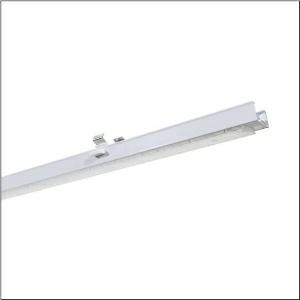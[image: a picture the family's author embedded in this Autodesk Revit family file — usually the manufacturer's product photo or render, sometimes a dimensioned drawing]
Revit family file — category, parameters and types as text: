
# Revit family: sanierungs-leuchteneinsatz_31_gen_2_51re11mb4cb_9c12
name_source: partatom
category: Lighting Fixtures
units: mm (PartAtom-declared; Revit-internal decimal feet)

## family parameters
Cut with Voids When Loaded = No
Host = Face
Light Source = No
Part Type = Normal
Room Calculation Point = No
Round Connector Dimension = Use Diameter
Shared = No

## types (1)
- --- (1 x LED, 11500 lm, 66 W, 4000K)
    Apparent Load = 66 VA
    CIE Flux Codes = 83 93 98 100 100
    Color Rendering = 80
    Color Temperature = 4000K
    Default Elevation = 1800 mm
    Description = Refurbishment luminaire insert Gen.2, luminaire insert, of extruded aluminium section, coated, traffic white (RAL 9016), length: 1.472mm, width: 91mm, height: 53mm, LED rated luminous flux: 11.500lm, light colour: 840, control gear: ON/OFF Multilumen, control gear: ECG Multilumen, with system connector: socket, mains connection: 220..240V, AC, 50/60Hz, connected load according to luminous flux setting (19/24/32/37/47/52/60/66W), luminous flux adjustable on luminaire in eight steps (3450/4380/5800/6700/8350/9200/10500/11500lm ), primary light control with lens, of plastic, primary optical cover: cover, of PMMA, light emission: direct distribution, protection rating (complete): IP20, insulation class (complete): insulation class I (protective earthing), certification: CE, UKCA, permissible ambient temperature for indoor applications: -20..+40°C, packaging unit: 1 piece
    Height = 58 mm
    Lamp = 1 x LED
    Lamp Light Flux = 11500 lm
    Lamp Power = 66 W
    Lamp count = 1
    Length = 1472 mm
    Luminous efficacy = 174 lm/W
    Manufacturer = Siteco
    ModVariant = No
    Model = 51RE11MB4CB
    Mounting Place = Ceiling
    Mounting Type = Pendant
    Number of Poles = 1
    OnlyDefault = Yes
    Power Factor = 1
    Product Name = Sanierungs-Leuchteneinsatz 31 Gen.2
    Product group = luminaire insert
    ProductGroupID = 902
    Protection Class = Protection class I
    Protection Degree = IP 20
    RLX_Detail_Level = 1
    RlxData = <blob elided: 21005 chars, md5=f5241e18>
    Socket = socket
    Standby Power = 0 W
    System Light Flux = 11500 lm
    System Power = 66 W
    Type Comments = factory setting: luminous flux: 100 % | (ON | ON | ON)
    Type Image = l_1266702.jpg
    URL = http://relux.com
    VarID = @adj_068025
    Voltage = 0 V
    Weight = 0.00 kg
    Width = 65 mm

## geometry (parser evidence)
native form markers: Blend x4, Sweep x12
no freeform markers — native parametric forms only
